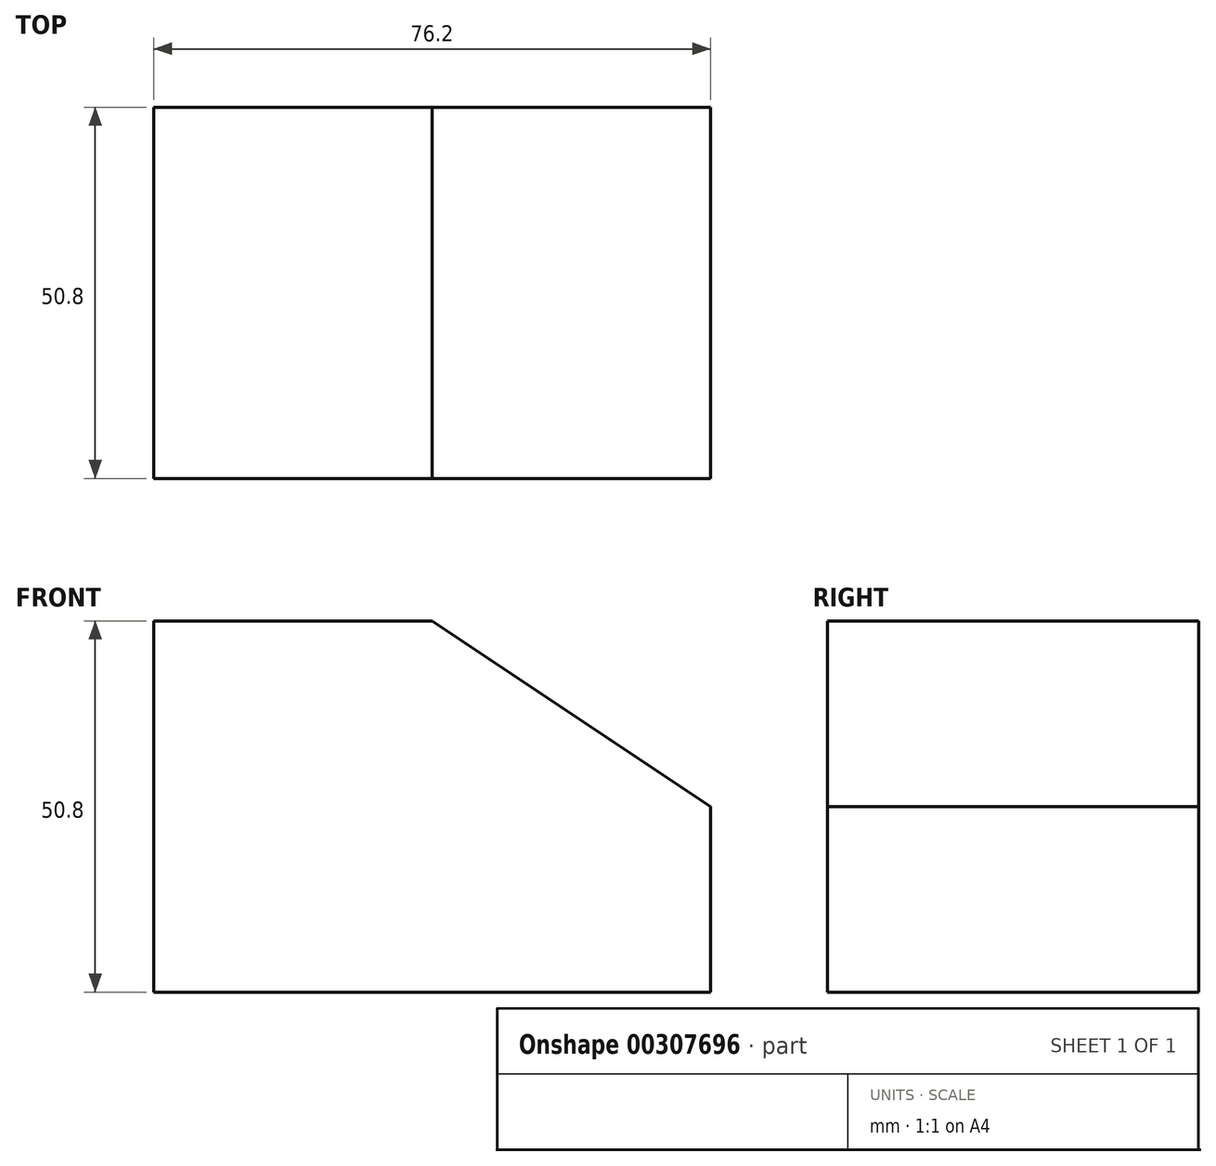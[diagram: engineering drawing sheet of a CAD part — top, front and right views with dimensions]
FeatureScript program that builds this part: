
annotation { "Feature Type Name" : "Feature", "Feature Type Description" : "" }
export const myFeature = defineFeature(function(context is Context, id is Id, definition is map)
    precondition{}
    {
        {
            var Q0;
            Q0=qCreatedBy(makeId("Front.planeOp"),FACE);
            var sketch = newSketch(context, id + "F0", { "sketchPlane" : qUnion([Q0])});
            skLineSegment(sketch, "E0", {"start": v(-49.93, -34.2) * mm, "end": v(26.27, -34.2) * mm});
            skLineSegment(sketch, "E1", {"start": v(26.27, -34.2) * mm, "end": v(26.27, -8.8) * mm});
            skLineSegment(sketch, "E2", {"start": v(26.27, -8.8) * mm, "end": v(-11.83, 16.6) * mm});
            skLineSegment(sketch, "E3", {"start": v(-11.83, 16.6) * mm, "end": v(-49.93, 16.6) * mm});
            skLineSegment(sketch, "E4", {"start": v(-49.93, 16.6) * mm, "end": v(-49.93, -34.2) * mm});
            skSolve(sketch);
        }
        {
            var Q0;
            Q0=makeQuery(id+"F0.imprint","IMPRINT",FACE,{"disambiguationData":[TD([[makeQuery(id+"F0.imprint","IMPRINT",EDGE,{"derivedFrom":sQuery(id+"F0.wireOp",EDGE,"E0")}),1.0]])]});
            extrude(context, id + "F1", {"entities" : qUnion([Q0]), "depth" : 50.8 * mm});
        }
    });
